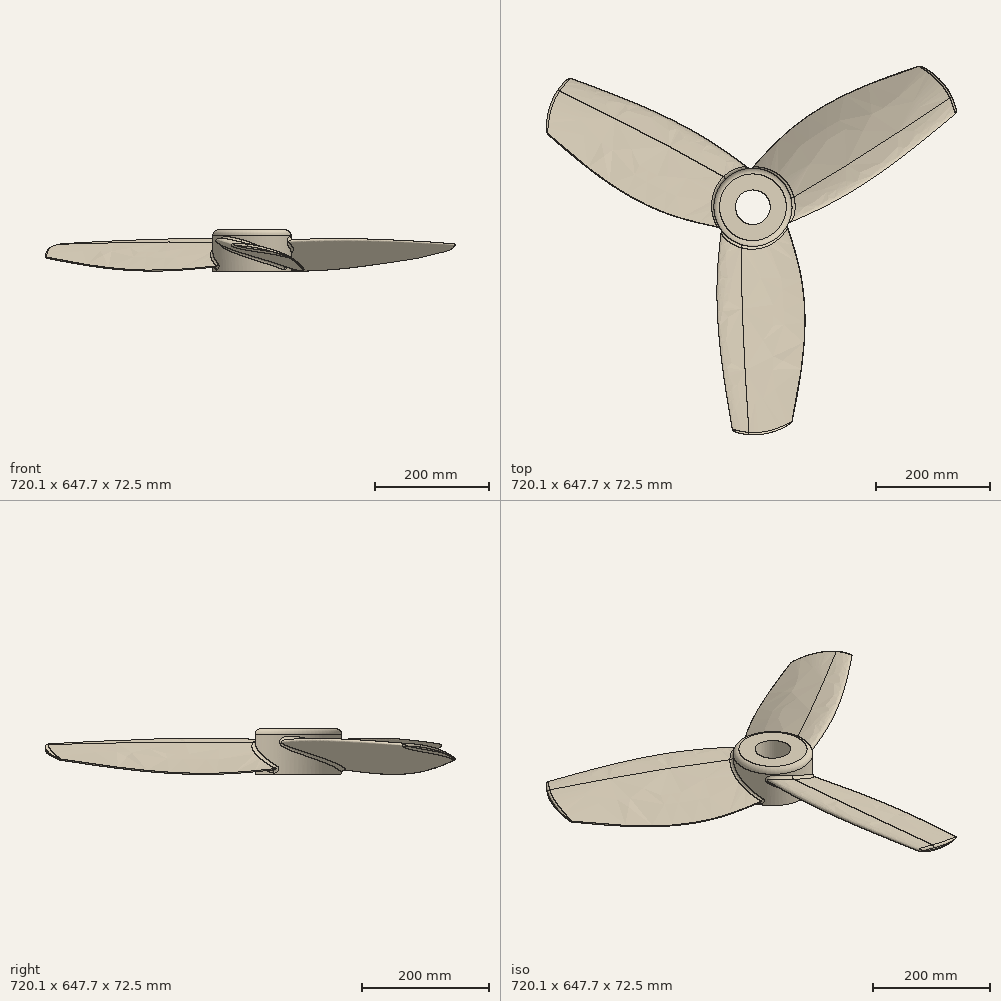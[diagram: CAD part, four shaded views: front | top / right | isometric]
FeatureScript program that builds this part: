
annotation { "Feature Type Name" : "Feature", "Feature Type Description" : "" }
export const myFeature = defineFeature(function(context is Context, id is Id, definition is map)
    precondition{}
    {
        {
            var Q0;
            Q0=qCreatedBy(makeId("Front.planeOp"),FACE);
            var sketch = newSketch(context, id + "F0", { "sketchPlane" : qUnion([Q0])});
            skLineSegment(sketch, "E0", {"start": v(-25.68, 10.16) * mm, "end": v(0, 0) * mm, "construction": true});
            skLineSegment(sketch, "E1", {"start": v(0, 0) * mm, "end": v(25.68, -10.16) * mm, "construction": true});
            skLineSegment(sketch, "E2", {"start": v(25.68, -10.16) * mm, "end": v(51.36, -20.31) * mm, "construction": true});
            skLineSegment(sketch, "E3", {"start": v(51.36, -20.31) * mm, "end": v(77.03, -30.47) * mm, "construction": true});
            skLineSegment(sketch, "E4", {"start": v(0, 0) * mm, "end": v(3.73, 9.44) * mm, "construction": true});
            skLineSegment(sketch, "E5", {"start": v(-25.68, 10.16) * mm, "end": v(-23.81, 14.88) * mm, "construction": true});
            skFitSpline(sketch, "E6", {"points": [v(-25.68, 10.16) * mm, v(3.73, 9.44) * mm, v(77.03, -30.47) * mm], "startDerivative": vector(15.03, 38) * mm, "endDerivative": vector(104.92, -93.69) * mm});
            skPoint(sketch, "E7", {"position": v(1.87, 4.72) * mm});
            skLineSegment(sketch, "E8", {"start": v(-23.81, 14.88) * mm, "end": v(1.87, 4.72) * mm, "construction": true});
            skLineSegment(sketch, "E9", {"start": v(0, 0) * mm, "end": v(-1.87, -4.72) * mm, "construction": true});
            skLineSegment(sketch, "E10", {"start": v(-25.68, 10.16) * mm, "end": v(-27.54, 5.44) * mm, "construction": true});
            skFitSpline(sketch, "E11", {"points": [v(-25.68, 10.16) * mm, v(-1.87, -4.72) * mm, v(77.03, -30.47) * mm], "startDerivative": vector(-15.23, -38.5) * mm, "endDerivative": vector(121.84, -48.19) * mm});
            skLineSegment(sketch, "E12", {"start": v(51.36, -20.31) * mm, "end": v(55.09, -10.87) * mm, "construction": true});
            skSolve(sketch);
        }
        {
            var Q0;
            Q0=qCreatedBy(makeId("Front.planeOp"),FACE);
            cPlane(context, id + "F1", {"entities" : qUnion([Q0]), "cplaneType" : CPlaneType.OFFSET, "offset" : 125 * mm, "width" : 150 * mm, "height" : 150 * mm});
        }
        {
            var Q0;
            Q0=qCreatedBy(id+"F1.planeOp",FACE);
            var sketch = newSketch(context, id + "F2", { "sketchPlane" : qUnion([Q0])});
            skLineSegment(sketch, "E13", {"start": v(-38.33, 14.06) * mm, "end": v(0, 0) * mm, "construction": true});
            skLineSegment(sketch, "E14", {"start": v(0, 0) * mm, "end": v(38.33, -14.06) * mm, "construction": true});
            skLineSegment(sketch, "E15", {"start": v(38.33, -14.06) * mm, "end": v(76.67, -28.12) * mm, "construction": true});
            skLineSegment(sketch, "E16", {"start": v(76.67, -28.12) * mm, "end": v(115, -42.17) * mm, "construction": true});
            skLineSegment(sketch, "E17", {"start": v(0, 0) * mm, "end": v(4.06, 11.06) * mm, "construction": true});
            skLineSegment(sketch, "E18", {"start": v(-38.33, 14.06) * mm, "end": v(-36.3, 19.59) * mm, "construction": true});
            skFitSpline(sketch, "E19", {"points": [v(-38.33, 14.06) * mm, v(4.06, 11.06) * mm, v(115, -42.17) * mm], "startDerivative": vector(16.44, 44.82) * mm, "endDerivative": vector(163.27, -119.63) * mm});
            skPoint(sketch, "E20", {"position": v(2.03, 5.53) * mm});
            skLineSegment(sketch, "E21", {"start": v(-36.3, 19.59) * mm, "end": v(2.03, 5.53) * mm, "construction": true});
            skLineSegment(sketch, "E22", {"start": v(0, 0) * mm, "end": v(-2.03, -5.53) * mm, "construction": true});
            skLineSegment(sketch, "E23", {"start": v(-38.33, 14.06) * mm, "end": v(-40.36, 8.53) * mm, "construction": true});
            skFitSpline(sketch, "E24", {"points": [v(-38.33, 14.06) * mm, v(-2.03, -5.53) * mm, v(115, -42.17) * mm], "startDerivative": vector(-16.57, -45.19) * mm, "endDerivative": vector(181.7, -66.64) * mm});
            skLineSegment(sketch, "E25", {"start": v(76.67, -28.12) * mm, "end": v(80.72, -17.06) * mm, "construction": true});
            skSolve(sketch);
        }
        {
            var Q0;
            Q0=qCreatedBy(makeId("Front.planeOp"),FACE);
            cPlane(context, id + "F3", {"entities" : qUnion([Q0]), "cplaneType" : CPlaneType.OFFSET, "offset" : 400 * mm, "width" : 150 * mm, "height" : 150 * mm});
        }
        {
            var Q0;
            Q0=qCreatedBy(id+"F3.planeOp",FACE);
            var sketch = newSketch(context, id + "F4", { "sketchPlane" : qUnion([Q0])});
            skLineSegment(sketch, "E26", {"start": v(-10.03, 5.14) * mm, "end": v(16.27, 0) * mm, "construction": true});
            skLineSegment(sketch, "E27", {"start": v(16.27, 0) * mm, "end": v(42.56, -5.14) * mm, "construction": true});
            skLineSegment(sketch, "E28", {"start": v(42.56, -5.14) * mm, "end": v(68.86, -10.28) * mm, "construction": true});
            skLineSegment(sketch, "E29", {"start": v(68.86, -10.28) * mm, "end": v(95.16, -15.42) * mm, "construction": true});
            skLineSegment(sketch, "E30", {"start": v(16.27, 0) * mm, "end": v(17.61, 6.9) * mm, "construction": true});
            skLineSegment(sketch, "E31", {"start": v(-10.03, 5.14) * mm, "end": v(-9.36, 8.59) * mm, "construction": true});
            skFitSpline(sketch, "E32", {"points": [v(-10.03, 5.14) * mm, v(17.61, 6.9) * mm, v(95.16, -15.42) * mm], "startDerivative": vector(5.47, 28.01) * mm, "endDerivative": vector(118.7, -57.28) * mm});
            skPoint(sketch, "E33", {"position": v(16.94, 3.45) * mm});
            skLineSegment(sketch, "E34", {"start": v(-9.36, 8.59) * mm, "end": v(16.94, 3.45) * mm, "construction": true});
            skLineSegment(sketch, "E35", {"start": v(16.27, 0) * mm, "end": v(15.6, -3.45) * mm, "construction": true});
            skLineSegment(sketch, "E36", {"start": v(-10.03, 5.14) * mm, "end": v(-10.7, 1.7) * mm, "construction": true});
            skFitSpline(sketch, "E37", {"points": [v(-10.03, 5.14) * mm, v(15.6, -3.45) * mm, v(95.16, -15.42) * mm], "startDerivative": vector(-5.51, -28.2) * mm, "endDerivative": vector(124.61, -24.36) * mm});
            skLineSegment(sketch, "E38", {"start": v(68.86, -10.28) * mm, "end": v(70.2, -3.38) * mm, "construction": true});
            skSolve(sketch);
        }
        {
            var Q0;
            Q0=qSketchRegion(id+"F0",true);
            var Q1;
            Q1=qSketchRegion(id+"F2",true);
            var Q2;
            Q2=qSketchRegion(id+"F4",true);
            var Q3;
            Q3=sQuery(id+"F0.wireOp",VERTEX,"E6.1.internal");
            var Q4;
            Q4=sQuery(id+"F2.wireOp",VERTEX,"E19.1.internal");
            var Q5;
            Q5=sQuery(id+"F4.wireOp",VERTEX,"E30.end");
            loft(context, id + "F5", {"sheetProfilesArray" : [{ "sheetProfileEntities" : qUnion([Q0]) }, { "sheetProfileEntities" : qUnion([Q1]) }, { "sheetProfileEntities" : qUnion([Q2]) }], "matchConnections" : true, "connections" : [{ "connectionEntities" : qUnion([Q3, Q4, Q5]), "connectionEdgeQueries" : qUnion([]), "connectionEdgeParameters" : [] }]});
        }
        {
            var Q0;
            Q0=qCreatedBy(makeId("Top.planeOp"),FACE);
            var sketch = newSketch(context, id + "F6", { "sketchPlane" : qUnion([Q0])});
            skFitSpline(sketch, "E39", {"points": [v(-55.98, -360.47) * mm, v(39.38, -398.87) * mm, v(142.8, -333.19) * mm], "startDerivative": vector(111.22, -150.8) * mm, "endDerivative": vector(54.24, 145.78) * mm});
            skLineSegment(sketch, "E40", {"start": v(-55.98, -360.47) * mm, "end": v(-55.98, -458.75) * mm});
            skLineSegment(sketch, "E41", {"start": v(142.8, -333.19) * mm, "end": v(142.8, -458.75) * mm});
            skLineSegment(sketch, "E42", {"start": v(142.8, -458.75) * mm, "end": v(-55.98, -458.75) * mm});
            skSolve(sketch);
        }
        {
            var Q0;
            Q0=qSketchRegion(id+"F6",true);
            extrude(context, id + "F7", {"entities" : qUnion([Q0]), "operationType" : NewBodyOperationType.REMOVE, "endBound" : BoundingType.SYMMETRIC, "oppositeDirection" : true, "depth" : 40.17 * mm, "offsetDistance" : 25 * mm});
        }
        {
            var Q0;
            Q0=makeQuery(id+"F5.opLoft","SWEPT_EDGE",EDGE,{"disambiguationData":[OSD([sQuery(id+"F2.wireOp",EDGE,"E19"),sQuery(id+"F2.wireOp",EDGE,"E24"),sQuery(id+"F4.wireOp",EDGE,"E32"),sQuery(id+"F4.wireOp",EDGE,"E37")])]});
            fillet(context, id + "F8", {"entities" : qUnion([Q0]), "radius" : 1 * mm, "tangentPropagation" : true, "allowEdgeOverflow" : false});
        }
        {
            var Q0;
            Q0=makeQuery(id+"F7.boolean.opBoolean","COPY",FACE,{"derivedFrom":makeQuery(id+"F7.opExtrude","SWEPT_FACE",FACE,{"disambiguationData":[OSD([sQuery(id+"F6.wireOp",EDGE,"E39")])]})});
            fillet(context, id + "F9", {"entities" : qUnion([Q0]), "radius" : 4 * mm, "tangentPropagation" : true, "allowEdgeOverflow" : false});
        }
        {
            var Q0;
            Q0=qCreatedBy(makeId("Top.planeOp"),FACE);
            var sketch = newSketch(context, id + "F10", { "sketchPlane" : qUnion([Q0])});
            skCircle(sketch, "E43", {"center": v(24.35, 0) * mm, "radius": 68.6 * mm});
            skSolve(sketch);
        }
        {
            var Q0;
            Q0=qSketchRegion(id+"F10",true);
            extrude(context, id + "F11", {"entities" : qUnion([Q0]), "depth" : 32.31 * mm, "hasSecondDirection" : true, "secondDirectionOppositeDirection" : true, "secondDirectionDepth" : 40 * mm});
        }
        {
            var Q0;
            Q0=makeQuery(id+"F5.opLoft","SWEPT_BODY",BODY,{"disambiguationData":[OSD([makeQuery(id+"F0.imprint","IMPRINT",FACE,{"disambiguationData":[TD([[makeQuery(id+"F0.imprint","IMPRINT",EDGE,{"derivedFrom":sQuery(id+"F0.wireOp",EDGE,"E6")}),-1.0]])]}),sQuery(id+"F2.wireOp",EDGE,"E24"),makeQuery(id+"F4.imprint","IMPRINT",FACE,{"disambiguationData":[TD([[makeQuery(id+"F4.imprint","IMPRINT",EDGE,{"derivedFrom":sQuery(id+"F4.wireOp",EDGE,"E32")}),-1.0]])]})])]});
            var Q1;
            Q1=makeQuery(id+"F11.opExtrude","SWEPT_FACE",FACE,{"disambiguationData":[OSD([sQuery(id+"F10.wireOp",EDGE,"E43")])]});
            circularPattern(context, id + "F12", {"entities" : qUnion([Q0]), "axis" : qUnion([Q1]), "angle" : 360 * degree, "instanceCount" : 3, "equalSpace" : true});
        }
        {
            var Q0;
            Q0=makeQuery(id+"F12.opPattern","COPY",BODY,{"derivedFrom":makeQuery(id+"F5.opLoft","SWEPT_BODY",BODY,{"disambiguationData":[OSD([makeQuery(id+"F0.imprint","IMPRINT",FACE,{"disambiguationData":[TD([[makeQuery(id+"F0.imprint","IMPRINT",EDGE,{"derivedFrom":sQuery(id+"F0.wireOp",EDGE,"E6")}),-1.0]])]}),sQuery(id+"F2.wireOp",EDGE,"E24"),makeQuery(id+"F4.imprint","IMPRINT",FACE,{"disambiguationData":[TD([[makeQuery(id+"F4.imprint","IMPRINT",EDGE,{"derivedFrom":sQuery(id+"F4.wireOp",EDGE,"E32")}),-1.0]])]})])]}),"instanceName":"2"});
            var Q1;
            Q1=makeQuery(id+"F5.opLoft","SWEPT_BODY",BODY,{"disambiguationData":[OSD([makeQuery(id+"F0.imprint","IMPRINT",FACE,{"disambiguationData":[TD([[makeQuery(id+"F0.imprint","IMPRINT",EDGE,{"derivedFrom":sQuery(id+"F0.wireOp",EDGE,"E6")}),-1.0]])]}),sQuery(id+"F2.wireOp",EDGE,"E24"),makeQuery(id+"F4.imprint","IMPRINT",FACE,{"disambiguationData":[TD([[makeQuery(id+"F4.imprint","IMPRINT",EDGE,{"derivedFrom":sQuery(id+"F4.wireOp",EDGE,"E32")}),-1.0]])]})])]});
            var Q2;
            Q2=makeQuery(id+"F11.opExtrude","SWEPT_BODY",BODY,{"disambiguationData":[OSD([sQuery(id+"F10.wireOp",EDGE,"E43")])]});
            var Q3;
            Q3=makeQuery(id+"F12.opPattern","COPY",BODY,{"derivedFrom":makeQuery(id+"F5.opLoft","SWEPT_BODY",BODY,{"disambiguationData":[OSD([makeQuery(id+"F0.imprint","IMPRINT",FACE,{"disambiguationData":[TD([[makeQuery(id+"F0.imprint","IMPRINT",EDGE,{"derivedFrom":sQuery(id+"F0.wireOp",EDGE,"E6")}),-1.0]])]}),sQuery(id+"F2.wireOp",EDGE,"E24"),makeQuery(id+"F4.imprint","IMPRINT",FACE,{"disambiguationData":[TD([[makeQuery(id+"F4.imprint","IMPRINT",EDGE,{"derivedFrom":sQuery(id+"F4.wireOp",EDGE,"E32")}),-1.0]])]})])]}),"instanceName":"1"});
            var Q4;
            Q4=makeQuery(id+"F12.opPattern","COPY",BODY,{"derivedFrom":makeQuery(id+"F5.opLoft","SWEPT_BODY",BODY,{"disambiguationData":[OSD([makeQuery(id+"F0.imprint","IMPRINT",FACE,{"disambiguationData":[TD([[makeQuery(id+"F0.imprint","IMPRINT",EDGE,{"derivedFrom":sQuery(id+"F0.wireOp",EDGE,"E6")}),-1.0]])]}),sQuery(id+"F2.wireOp",EDGE,"E24"),makeQuery(id+"F4.imprint","IMPRINT",FACE,{"disambiguationData":[TD([[makeQuery(id+"F4.imprint","IMPRINT",EDGE,{"derivedFrom":sQuery(id+"F4.wireOp",EDGE,"E32")}),-1.0]])]})])]}),"instanceName":"4"});
            var Q5;
            Q5=makeQuery(id+"F12.opPattern","COPY",BODY,{"derivedFrom":makeQuery(id+"F5.opLoft","SWEPT_BODY",BODY,{"disambiguationData":[OSD([makeQuery(id+"F0.imprint","IMPRINT",FACE,{"disambiguationData":[TD([[makeQuery(id+"F0.imprint","IMPRINT",EDGE,{"derivedFrom":sQuery(id+"F0.wireOp",EDGE,"E6")}),-1.0]])]}),sQuery(id+"F2.wireOp",EDGE,"E24"),makeQuery(id+"F4.imprint","IMPRINT",FACE,{"disambiguationData":[TD([[makeQuery(id+"F4.imprint","IMPRINT",EDGE,{"derivedFrom":sQuery(id+"F4.wireOp",EDGE,"E32")}),-1.0]])]})])]}),"instanceName":"3"});
            booleanBodies(context, id + "F13", {"operationType" : BooleanOperationType.UNION, "tools" : qUnion([Q0, Q1, Q2, Q3, Q4, Q5])});
        }
        {
            var Q0;
            Q0=makeQuery(id+"F11.opExtrude","CAP_FACE",FACE,{"disambiguationData":[OSD([sQuery(id+"F10.wireOp",EDGE,"E43")])],"isStart":false});
            var sketch = newSketch(context, id + "F14", { "sketchPlane" : qUnion([Q0])});
            skCircle(sketch, "E44", {"center": v(24.35, 0) * mm, "radius": 30.45 * mm});
            skSolve(sketch);
        }
        {
            var Q0;
            Q0=qSketchRegion(id+"F14",true);
            extrude(context, id + "F15", {"entities" : qUnion([Q0]), "operationType" : NewBodyOperationType.REMOVE, "endBound" : BoundingType.THROUGH_ALL, "oppositeDirection" : true, "depth" : 25 * mm});
        }
        {
            var Q0;
            {var subQ0=sQuery(id+"F0.wireOp",VERTEX,"E6.1.internal");var subQ1=sQuery(id+"F0.wireOp",EDGE,"E6");var subQ2=sQuery(id+"F0.wireOp",EDGE,"E11");var subQ3=sQuery(id+"F2.wireOp",VERTEX,"E19.1.internal");var subQ4=sQuery(id+"F2.wireOp",EDGE,"E19");var subQ5=sQuery(id+"F2.wireOp",EDGE,"E24");Q0=makeQuery(id+"F13.opBoolean","INTERSECT",EDGE,{"derivedFrom":[makeQuery(id+"F11.opExtrude","SWEPT_FACE",FACE,{"disambiguationData":[OSD([sQuery(id+"F10.wireOp",EDGE,"E43")])]}),makeQuery(id+"F12.opPattern","COPY",FACE,{"derivedFrom":makeQuery(id+"F5.opLoft","SWEPT_FACE",FACE,{"disambiguationData":[OSD([subQ0,subQ1,subQ2,subQ3,subQ4,subQ5]),TDD([subQ0,makeQuery(id+"F0.imprint","INTERSECT",VERTEX,{"disambiguationData":[OD(0.0)],"derivedFrom":[subQ1,subQ2]}),makeQuery(id+"F0.imprint","IMPRINT",EDGE,{"derivedFrom":subQ1}),subQ3,makeQuery(id+"F2.imprint","INTERSECT",VERTEX,{"disambiguationData":[OD(0.0)],"derivedFrom":[subQ4,subQ5]}),makeQuery(id+"F2.imprint","IMPRINT",EDGE,{"derivedFrom":subQ4})])]}),"instanceName":"2"})]});}
            var Q1;
            {var subQ0=sQuery(id+"F0.wireOp",VERTEX,"E6.1.internal");var subQ1=sQuery(id+"F0.wireOp",EDGE,"E6");var subQ2=sQuery(id+"F0.wireOp",EDGE,"E11");var subQ3=sQuery(id+"F2.wireOp",VERTEX,"E19.1.internal");var subQ4=sQuery(id+"F2.wireOp",EDGE,"E19");var subQ5=sQuery(id+"F2.wireOp",EDGE,"E24");Q1=makeQuery(id+"F13.opBoolean","INTERSECT",EDGE,{"derivedFrom":[makeQuery(id+"F5.opLoft","SWEPT_FACE",FACE,{"disambiguationData":[OSD([subQ0,subQ1,subQ2,subQ3,subQ4,subQ5]),TDD([subQ0,makeQuery(id+"F0.imprint","INTERSECT",VERTEX,{"disambiguationData":[OD(1.0)],"derivedFrom":[subQ1,subQ2]}),makeQuery(id+"F0.imprint","IMPRINT",EDGE,{"derivedFrom":subQ1}),subQ3,makeQuery(id+"F2.imprint","INTERSECT",VERTEX,{"disambiguationData":[OD(1.0)],"derivedFrom":[subQ4,subQ5]}),makeQuery(id+"F2.imprint","IMPRINT",EDGE,{"derivedFrom":subQ4})])]}),makeQuery(id+"F11.opExtrude","SWEPT_FACE",FACE,{"disambiguationData":[OSD([sQuery(id+"F10.wireOp",EDGE,"E43")])]})]});}
            var Q2;
            {var subQ0=sQuery(id+"F0.wireOp",VERTEX,"E6.1.internal");var subQ1=sQuery(id+"F0.wireOp",EDGE,"E6");var subQ2=sQuery(id+"F0.wireOp",EDGE,"E11");var subQ3=sQuery(id+"F2.wireOp",VERTEX,"E19.1.internal");var subQ4=sQuery(id+"F2.wireOp",EDGE,"E19");var subQ5=sQuery(id+"F2.wireOp",EDGE,"E24");Q2=makeQuery(id+"F13.opBoolean","INTERSECT",EDGE,{"derivedFrom":[makeQuery(id+"F11.opExtrude","SWEPT_FACE",FACE,{"disambiguationData":[OSD([sQuery(id+"F10.wireOp",EDGE,"E43")])]}),makeQuery(id+"F12.opPattern","COPY",FACE,{"derivedFrom":makeQuery(id+"F5.opLoft","SWEPT_FACE",FACE,{"disambiguationData":[OSD([subQ0,subQ1,subQ2,subQ3,subQ4,subQ5]),TDD([subQ0,makeQuery(id+"F0.imprint","INTERSECT",VERTEX,{"disambiguationData":[OD(1.0)],"derivedFrom":[subQ1,subQ2]}),makeQuery(id+"F0.imprint","IMPRINT",EDGE,{"derivedFrom":subQ1}),subQ3,makeQuery(id+"F2.imprint","INTERSECT",VERTEX,{"disambiguationData":[OD(1.0)],"derivedFrom":[subQ4,subQ5]}),makeQuery(id+"F2.imprint","IMPRINT",EDGE,{"derivedFrom":subQ4})])]}),"instanceName":"1"})]});}
            var Q3;
            {var subQ0=sQuery(id+"F0.wireOp",VERTEX,"E6.1.internal");var subQ1=sQuery(id+"F0.wireOp",EDGE,"E6");var subQ2=sQuery(id+"F0.wireOp",EDGE,"E11");var subQ3=sQuery(id+"F2.wireOp",VERTEX,"E19.1.internal");var subQ4=sQuery(id+"F2.wireOp",EDGE,"E19");var subQ5=sQuery(id+"F2.wireOp",EDGE,"E24");Q3=makeQuery(id+"F13.opBoolean","INTERSECT",EDGE,{"derivedFrom":[makeQuery(id+"F11.opExtrude","SWEPT_FACE",FACE,{"disambiguationData":[OSD([sQuery(id+"F10.wireOp",EDGE,"E43")])]}),makeQuery(id+"F12.opPattern","COPY",FACE,{"derivedFrom":makeQuery(id+"F5.opLoft","SWEPT_FACE",FACE,{"disambiguationData":[OSD([subQ0,subQ1,subQ2,subQ3,subQ4,subQ5]),TDD([subQ0,makeQuery(id+"F0.imprint","INTERSECT",VERTEX,{"disambiguationData":[OD(1.0)],"derivedFrom":[subQ1,subQ2]}),makeQuery(id+"F0.imprint","IMPRINT",EDGE,{"derivedFrom":subQ1}),subQ3,makeQuery(id+"F2.imprint","INTERSECT",VERTEX,{"disambiguationData":[OD(1.0)],"derivedFrom":[subQ4,subQ5]}),makeQuery(id+"F2.imprint","IMPRINT",EDGE,{"derivedFrom":subQ4})])]}),"instanceName":"4"})]});}
            var Q4;
            {var subQ0=sQuery(id+"F0.wireOp",VERTEX,"E6.1.internal");var subQ1=sQuery(id+"F0.wireOp",EDGE,"E6");var subQ2=sQuery(id+"F0.wireOp",EDGE,"E11");var subQ3=sQuery(id+"F2.wireOp",VERTEX,"E19.1.internal");var subQ4=sQuery(id+"F2.wireOp",EDGE,"E19");var subQ5=sQuery(id+"F2.wireOp",EDGE,"E24");Q4=makeQuery(id+"F13.opBoolean","INTERSECT",EDGE,{"derivedFrom":[makeQuery(id+"F11.opExtrude","SWEPT_FACE",FACE,{"disambiguationData":[OSD([sQuery(id+"F10.wireOp",EDGE,"E43")])]}),makeQuery(id+"F12.opPattern","COPY",FACE,{"derivedFrom":makeQuery(id+"F5.opLoft","SWEPT_FACE",FACE,{"disambiguationData":[OSD([subQ0,subQ1,subQ2,subQ3,subQ4,subQ5]),TDD([subQ0,makeQuery(id+"F0.imprint","INTERSECT",VERTEX,{"disambiguationData":[OD(0.0)],"derivedFrom":[subQ1,subQ2]}),makeQuery(id+"F0.imprint","IMPRINT",EDGE,{"derivedFrom":subQ1}),subQ3,makeQuery(id+"F2.imprint","INTERSECT",VERTEX,{"disambiguationData":[OD(0.0)],"derivedFrom":[subQ4,subQ5]}),makeQuery(id+"F2.imprint","IMPRINT",EDGE,{"derivedFrom":subQ4})])]}),"instanceName":"3"})]});}
            fillet(context, id + "F16", {"entities" : qUnion([Q0, Q1, Q2, Q3, Q4]), "radius" : 5 * mm, "tangentPropagation" : true, "allowEdgeOverflow" : false});
        }
        {
            var Q0;
            Q0=makeQuery(id+"F11.opExtrude","CAP_EDGE",EDGE,{"disambiguationData":[OSD([sQuery(id+"F10.wireOp",EDGE,"E43")])],"isStart":false});
            fillet(context, id + "F17", {"entities" : qUnion([Q0]), "radius" : 10 * mm, "tangentPropagation" : true, "allowEdgeOverflow" : false});
        }
    });
